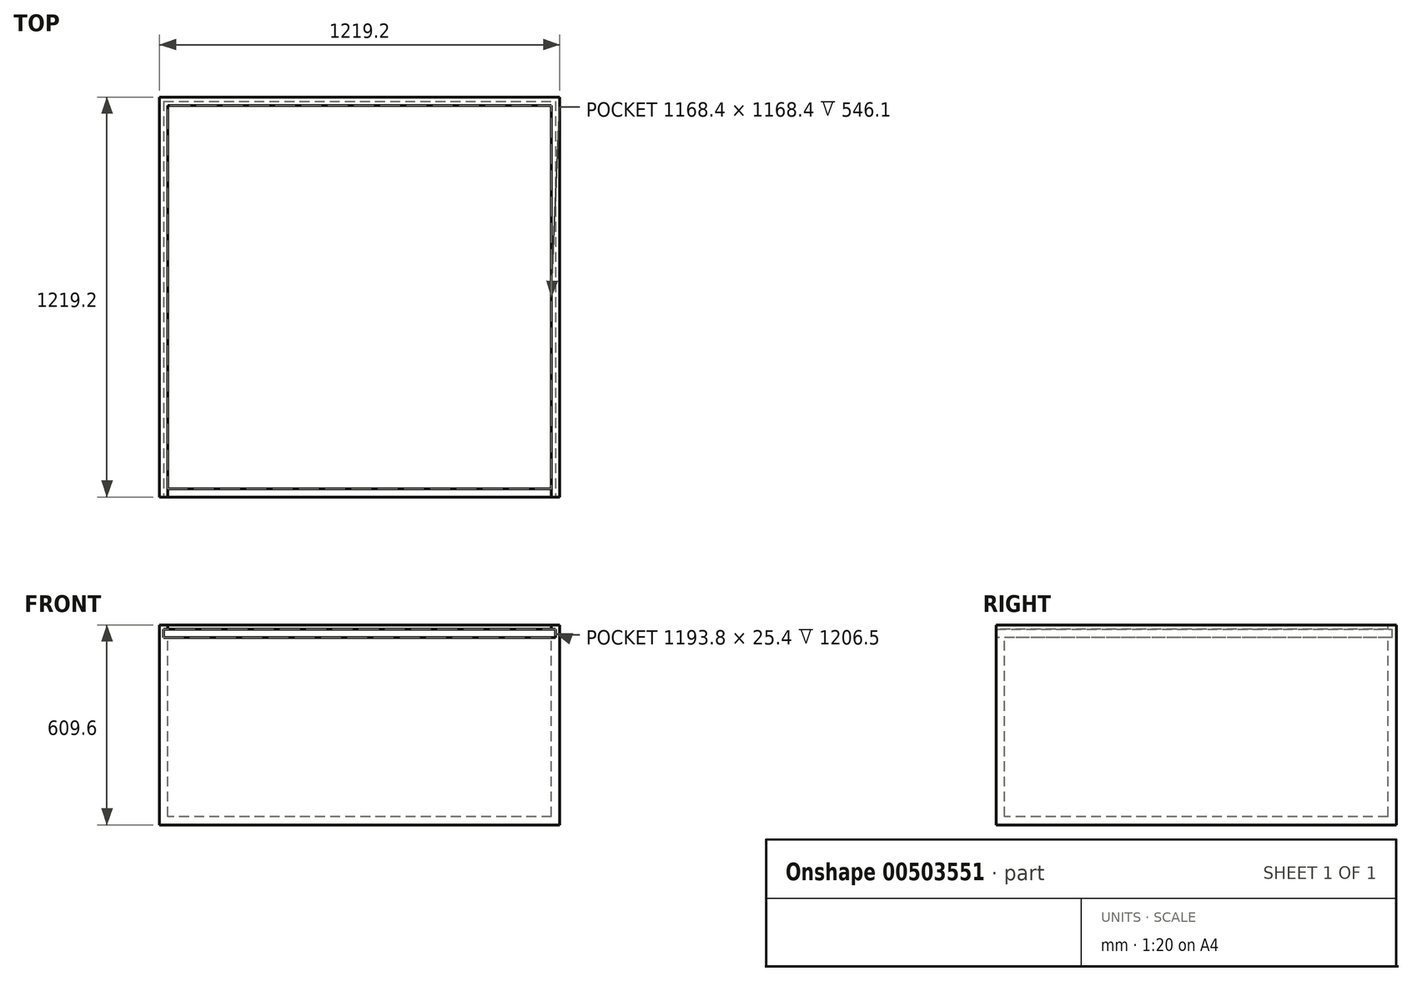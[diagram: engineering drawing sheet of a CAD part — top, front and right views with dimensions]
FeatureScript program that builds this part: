
annotation { "Feature Type Name" : "Feature", "Feature Type Description" : "" }
export const myFeature = defineFeature(function(context is Context, id is Id, definition is map)
    precondition{}
    {
        {
            var Q0;
            Q0=qCreatedBy(makeId("Front.planeOp"),FACE);
            var sketch = newSketch(context, id + "F0", { "sketchPlane" : qUnion([Q0])});
            skLineSegment(sketch, "E0.bottom", {"start": v(609.6, 304.8) * mm, "end": v(-609.6, 304.8) * mm});
            skLineSegment(sketch, "E0.top", {"start": v(609.6, -304.8) * mm, "end": v(-609.6, -304.8) * mm});
            skLineSegment(sketch, "E0.left", {"start": v(609.6, 304.8) * mm, "end": v(609.6, -304.8) * mm});
            skLineSegment(sketch, "E0.right", {"start": v(-609.6, 304.8) * mm, "end": v(-609.6, -304.8) * mm});
            skPoint(sketch, "E0.middle", {"position": v(0, 0) * mm});
            skSolve(sketch);
        }
        {
            var Q0;
            Q0=makeQuery(id+"F0.imprint","IMPRINT",FACE,{"disambiguationData":[TD([[makeQuery(id+"F0.imprint","IMPRINT",EDGE,{"derivedFrom":sQuery(id+"F0.wireOp",EDGE,"E0.bottom")}),1.0]])]});
            extrude(context, id + "F1", {"entities" : qUnion([Q0]), "endBound" : BoundingType.SYMMETRIC, "depth" : 1219.2 * mm});
        }
        {
            var Q0;
            Q0=makeQuery(id+"F1.opExtrude","SWEPT_FACE",FACE,{"disambiguationData":[OSD([sQuery(id+"F0.wireOp",EDGE,"E0.bottom")])]});
            var sketch = newSketch(context, id + "F2", { "sketchPlane" : qUnion([Q0])});
            skLineSegment(sketch, "E1.bottom", {"start": v(584.2, 584.2) * mm, "end": v(-584.2, 584.2) * mm});
            skLineSegment(sketch, "E1.top", {"start": v(584.2, -584.2) * mm, "end": v(-584.2, -584.2) * mm});
            skLineSegment(sketch, "E1.left", {"start": v(584.2, 584.2) * mm, "end": v(584.2, -584.2) * mm});
            skLineSegment(sketch, "E1.right", {"start": v(-584.2, 584.2) * mm, "end": v(-584.2, -584.2) * mm});
            skPoint(sketch, "E1.middle", {"position": v(0, 0) * mm});
            skSolve(sketch);
        }
        {
            var Q0;
            Q0=makeQuery(id+"F2.imprint","IMPRINT",FACE,{"disambiguationData":[TD([[makeQuery(id+"F2.imprint","IMPRINT",EDGE,{"derivedFrom":sQuery(id+"F2.wireOp",EDGE,"E1.bottom")}),1.0]])]});
            extrude(context, id + "F3", {"entities" : qUnion([Q0]), "operationType" : NewBodyOperationType.REMOVE, "oppositeDirection" : true, "depth" : 584.2 * mm});
        }
        {
            var Q0;
            Q0=makeQuery(id+"F1.opExtrude","SWEPT_FACE",FACE,{"disambiguationData":[OSD([sQuery(id+"F0.wireOp",EDGE,"E0.bottom")])]});
            var sketch = newSketch(context, id + "F4", { "sketchPlane" : qUnion([Q0])});
            skLineSegment(sketch, "E2.bottom", {"start": v(-584.2, -584.2) * mm, "end": v(584.2, -584.2) * mm});
            skLineSegment(sketch, "E2.top", {"start": v(-584.2, -609.6) * mm, "end": v(584.2, -609.6) * mm});
            skLineSegment(sketch, "E2.left", {"start": v(-584.2, -584.2) * mm, "end": v(-584.2, -609.6) * mm});
            skLineSegment(sketch, "E2.right", {"start": v(584.2, -584.2) * mm, "end": v(584.2, -609.6) * mm});
            skSolve(sketch);
        }
        {
            var Q0;
            Q0=makeQuery(id+"F4.imprint","IMPRINT",FACE,{"disambiguationData":[TD([[makeQuery(id+"F4.imprint","IMPRINT",EDGE,{"derivedFrom":sQuery(id+"F4.wireOp",EDGE,"E2.bottom")}),1.0]])]});
            extrude(context, id + "F5", {"entities" : qUnion([Q0]), "operationType" : NewBodyOperationType.REMOVE, "oppositeDirection" : true, "depth" : 38.1 * mm});
        }
        {
            var Q0;
            Q0=makeQuery(id+"F5.boolean.opBoolean","MERGE",FACE,{"derivedFrom":[makeQuery(id+"F3.boolean.opBoolean","COPY",FACE,{"derivedFrom":makeQuery(id+"F3.opExtrude","SWEPT_FACE",FACE,{"disambiguationData":[OSD([sQuery(id+"F2.wireOp",EDGE,"E1.right")])]})}),makeQuery(id+"F5.opExtrude","SWEPT_FACE",FACE,{"disambiguationData":[OSD([sQuery(id+"F4.wireOp",EDGE,"E2.left")])]})]});
            var sketch = newSketch(context, id + "F6", { "sketchPlane" : qUnion([Q0])});
            skPoint(sketch, "E3.oppositeSnap0", {"position": v(-609.6, 292.1) * mm});
            skLineSegment(sketch, "E3.bottom", {"start": v(-609.6, 266.7) * mm, "end": v(596.9, 266.7) * mm});
            skLineSegment(sketch, "E3.top", {"start": v(-609.6, 292.1) * mm, "end": v(596.9, 292.1) * mm});
            skLineSegment(sketch, "E3.left", {"start": v(-609.6, 266.7) * mm, "end": v(-609.6, 292.1) * mm});
            skLineSegment(sketch, "E3.right", {"start": v(596.9, 266.7) * mm, "end": v(596.9, 285.75) * mm});
            skSolve(sketch);
        }
        {
            var Q0;
            {var subQ0=sQuery(id+"F6.wireOp",EDGE,"E3.left");Q0=makeQuery(id+"F6.imprint","IMPRINT",FACE,{"disambiguationData":[TD([[makeQuery(id+"F6.imprint","IMPRINT",EDGE,{"derivedFrom":subQ0}),-1.0]])]});}
            extrude(context, id + "F7", {"entities" : qUnion([Q0]), "operationType" : NewBodyOperationType.REMOVE, "oppositeDirection" : true, "depth" : 12.7 * mm});
        }
        {
            var Q0;
            {var subQ0=sQuery(id+"F2.wireOp",EDGE,"E1.bottom");Q0=makeQuery(id+"F7.boolean.opBoolean","MERGE",FACE,{"derivedFrom":[makeQuery(id+"F3.boolean.opBoolean","COPY",FACE,{"derivedFrom":makeQuery(id+"F3.opExtrude","SWEPT_FACE",FACE,{"disambiguationData":[OSD([subQ0])]})}),makeQuery(id+"F7.opExtrude","SWEPT_FACE",FACE,{"disambiguationData":[OSD([subQ0,sQuery(id+"F2.wireOp",EDGE,"E1.right")])]})]});}
            var sketch = newSketch(context, id + "F8", { "sketchPlane" : qUnion([Q0])});
            skLineSegment(sketch, "E4.bottom", {"start": v(-596.9, 266.7) * mm, "end": v(596.9, 266.7) * mm});
            skLineSegment(sketch, "E4.top", {"start": v(-596.9, 292.1) * mm, "end": v(596.9, 292.1) * mm});
            skLineSegment(sketch, "E4.left", {"start": v(-596.9, 266.7) * mm, "end": v(-596.9, 292.1) * mm});
            skLineSegment(sketch, "E4.right", {"start": v(596.9, 266.7) * mm, "end": v(596.9, 292.1) * mm});
            skSolve(sketch);
        }
        {
            var Q0;
            {var subQ10=sQuery(id+"F8.wireOp",EDGE,"E4.left");Q0=makeQuery(id+"F8.imprint","IMPRINT",FACE,{"disambiguationData":[TD([[makeQuery(id+"F8.imprint","IMPRINT",EDGE,{"derivedFrom":subQ10}),-1.0]])]});}
            extrude(context, id + "F9", {"entities" : qUnion([Q0]), "operationType" : NewBodyOperationType.REMOVE, "oppositeDirection" : true, "depth" : 12.7 * mm});
        }
        {
            var Q0;
            {var subQ0=sQuery(id+"F2.wireOp",EDGE,"E1.left");Q0=makeQuery(id+"F9.boolean.opBoolean","MERGE",FACE,{"derivedFrom":[makeQuery(id+"F5.boolean.opBoolean","MERGE",FACE,{"derivedFrom":[makeQuery(id+"F3.boolean.opBoolean","COPY",FACE,{"derivedFrom":makeQuery(id+"F3.opExtrude","SWEPT_FACE",FACE,{"disambiguationData":[OSD([subQ0])]})}),makeQuery(id+"F5.opExtrude","SWEPT_FACE",FACE,{"disambiguationData":[OSD([sQuery(id+"F4.wireOp",EDGE,"E2.right")])]})]}),makeQuery(id+"F9.opExtrude","SWEPT_FACE",FACE,{"disambiguationData":[OSD([sQuery(id+"F2.wireOp",EDGE,"E1.bottom"),subQ0])]})]});}
            var sketch = newSketch(context, id + "F10", { "sketchPlane" : qUnion([Q0])});
            skLineSegment(sketch, "E5.bottom", {"start": v(-596.9, 266.7) * mm, "end": v(609.6, 266.7) * mm});
            skLineSegment(sketch, "E5.top", {"start": v(-596.9, 292.1) * mm, "end": v(609.6, 292.1) * mm});
            skLineSegment(sketch, "E5.left", {"start": v(-596.9, 266.7) * mm, "end": v(-596.9, 292.1) * mm});
            skLineSegment(sketch, "E5.right", {"start": v(609.6, 266.7) * mm, "end": v(609.6, 292.1) * mm});
            skSolve(sketch);
        }
        {
            var Q0;
            {var subQ18=sQuery(id+"F10.wireOp",EDGE,"E5.left");Q0=makeQuery(id+"F10.imprint","IMPRINT",FACE,{"disambiguationData":[TD([[makeQuery(id+"F10.imprint","IMPRINT",EDGE,{"derivedFrom":subQ18}),-1.0]])]});}
            extrude(context, id + "F11", {"entities" : qUnion([Q0]), "operationType" : NewBodyOperationType.REMOVE, "oppositeDirection" : true, "depth" : 12.7 * mm});
        }
    });
